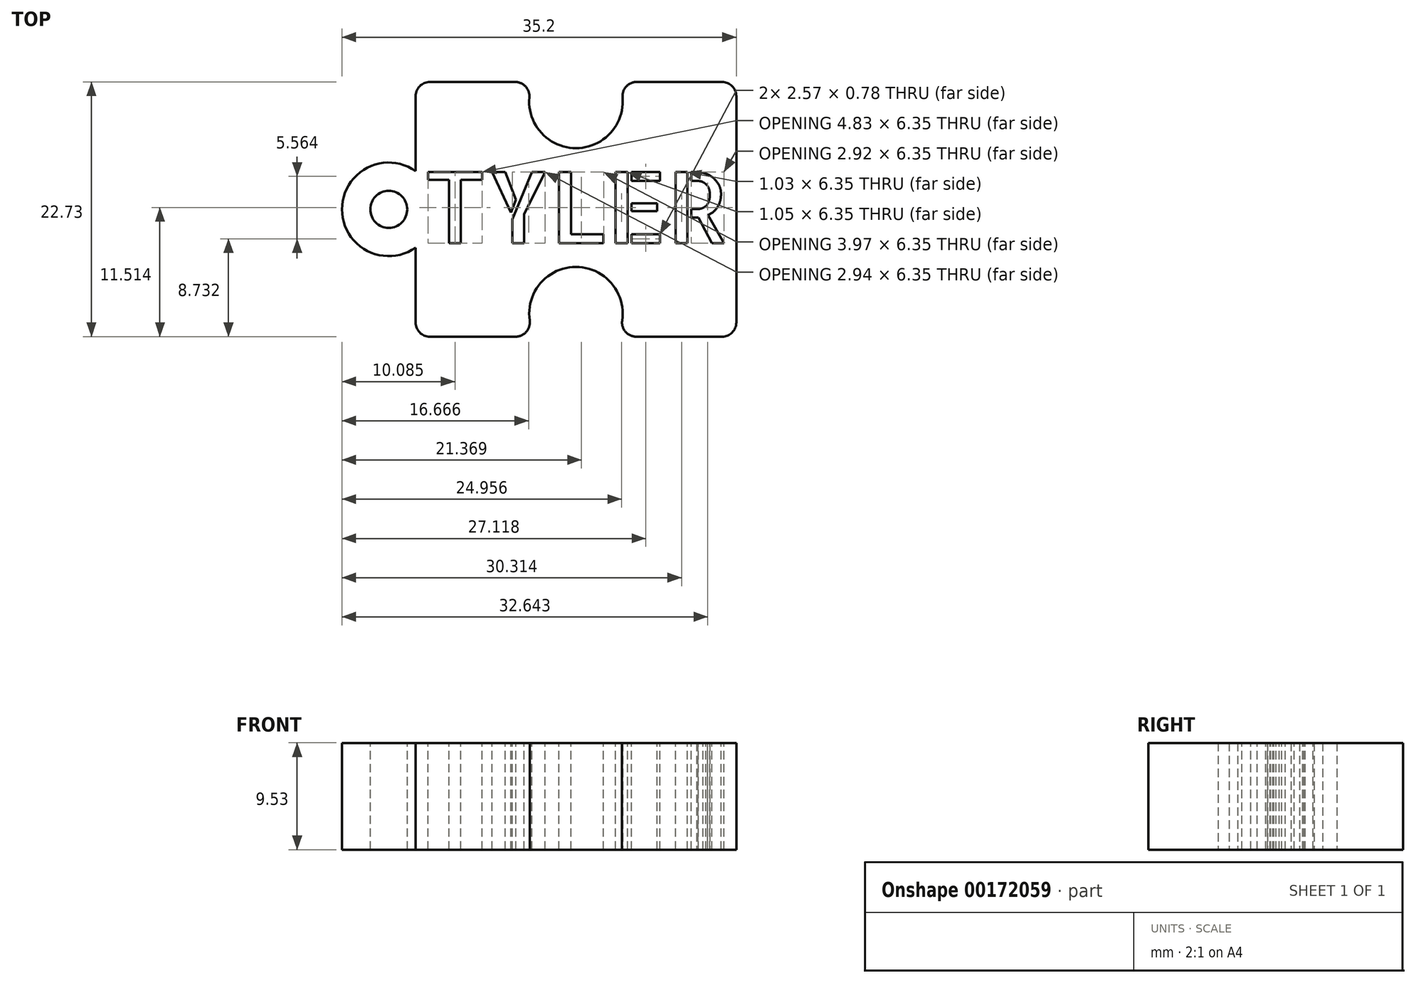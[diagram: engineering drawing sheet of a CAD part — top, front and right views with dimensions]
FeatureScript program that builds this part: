
annotation { "Feature Type Name" : "Feature", "Feature Type Description" : "" }
export const myFeature = defineFeature(function(context is Context, id is Id, definition is map)
    precondition{}
    {
        {
            var Q0;
            Q0=qCreatedBy(makeId("Top.planeOp"),FACE);
            var sketch = newSketch(context, id + "F0", { "sketchPlane" : qUnion([Q0])});
            skLineSegment(sketch, "E0.bottom", {"start": v(-24.82, 39.35) * mm, "end": v(-17.2, 39.35) * mm});
            skLineSegment(sketch, "E0.top", {"start": v(-24.82, 16.62) * mm, "end": v(-17.16, 16.62) * mm});
            skLineSegment(sketch, "E0.left", {"start": v(-26.09, 38.08) * mm, "end": v(-26.09, 31.4) * mm});
            skLineSegment(sketch, "E0.right", {"start": v(2.54, 38.08) * mm, "end": v(2.54, 17.89) * mm});
            skArc(sketch, "E1", {"start": v(-26.09, 31.4) * mm, "mid": v(-32.66, 27.98) * mm, "end": v(-26.09, 24.56) * mm});
            skArc(sketch, "E2", {"start": v(-7.65, 18.07) * mm, "mid": v(-11.78, 22.84) * mm, "end": v(-15.9, 18.07) * mm});
            skArc(sketch, "E3", {"start": v(-15.93, 37.97) * mm, "mid": v(-11.78, 33.44) * mm, "end": v(-7.62, 37.97) * mm});
            skLineSegment(sketch, "E4.trimOffspring", {"start": v(-6.35, 39.35) * mm, "end": v(1.27, 39.35) * mm});
            skLineSegment(sketch, "E5.trimOffspring", {"start": v(-6.39, 16.62) * mm, "end": v(1.27, 16.62) * mm});
            skLineSegment(sketch, "E6.trimOffspring", {"start": v(-26.09, 24.56) * mm, "end": v(-26.09, 17.89) * mm});
            skPoint(sketch, "E7", {"position": v(-11.78, 39.35) * mm});
            skPoint(sketch, "E8", {"position": v(-11.78, 16.62) * mm});
            skLineSegment(sketch, "E9", {"start": v(-11.78, 39.35) * mm, "end": v(-11.78, 16.62) * mm, "construction": true});
            skPoint(sketch, "E10.visualSharp", {"position": v(-26.09, 16.62) * mm});
            skArc(sketch, "E10.filletArc", {"start": v(-26.09, 17.89) * mm, "mid": v(-25.72, 16.99) * mm, "end": v(-24.82, 16.62) * mm});
            skPoint(sketch, "E11.visualSharp", {"position": v(-26.09, 39.35) * mm});
            skArc(sketch, "E11.filletArc", {"start": v(-24.82, 39.35) * mm, "mid": v(-25.72, 38.97) * mm, "end": v(-26.09, 38.08) * mm});
            skPoint(sketch, "E12.visualSharp", {"position": v(2.54, 39.35) * mm});
            skArc(sketch, "E12.filletArc", {"start": v(2.54, 38.08) * mm, "mid": v(2.16, 38.97) * mm, "end": v(1.27, 39.35) * mm});
            skPoint(sketch, "E13.visualSharp", {"position": v(2.54, 16.62) * mm});
            skArc(sketch, "E13.filletArc", {"start": v(1.27, 16.62) * mm, "mid": v(2.16, 16.99) * mm, "end": v(2.54, 17.89) * mm});
            skPoint(sketch, "E14.visualSharp", {"position": v(-8.14, 16.62) * mm});
            skArc(sketch, "E14.filletArc", {"start": v(-7.65, 18.07) * mm, "mid": v(-7.35, 17.05) * mm, "end": v(-6.39, 16.62) * mm});
            skPoint(sketch, "E15.visualSharp", {"position": v(-15.4, 16.62) * mm});
            skArc(sketch, "E15.filletArc", {"start": v(-17.16, 16.62) * mm, "mid": v(-16.2, 17.05) * mm, "end": v(-15.9, 18.07) * mm});
            skPoint(sketch, "E16.visualSharp", {"position": v(-7.98, 39.35) * mm});
            skArc(sketch, "E16.filletArc", {"start": v(-6.35, 39.35) * mm, "mid": v(-7.29, 38.93) * mm, "end": v(-7.62, 37.97) * mm});
            skPoint(sketch, "E17.visualSharp", {"position": v(-15.57, 39.35) * mm});
            skArc(sketch, "E17.filletArc", {"start": v(-15.93, 37.97) * mm, "mid": v(-16.26, 38.93) * mm, "end": v(-17.2, 39.35) * mm});
            skSolve(sketch);
        }
        {
            var Q0;
            Q0 = qSketchRegion(id + "F0", true);
            extrude(context, id + "F1", {"entities" : qUnion([Q0]), "depth" : 9.52 * mm});
        }
        {
            var Q0;
            Q0=makeQuery(id+"F1.opExtrude","CAP_FACE",FACE,{"disambiguationData":[OSD([sQuery(id+"F0.wireOp",EDGE,"E0.bottom"),sQuery(id+"F0.wireOp",EDGE,"E0.top"),sQuery(id+"F0.wireOp",EDGE,"E0.left"),sQuery(id+"F0.wireOp",EDGE,"E0.right"),sQuery(id+"F0.wireOp",EDGE,"E1"),sQuery(id+"F0.wireOp",EDGE,"E2"),sQuery(id+"F0.wireOp",EDGE,"E3"),sQuery(id+"F0.wireOp",EDGE,"E4.trimOffspring"),sQuery(id+"F0.wireOp",EDGE,"E5.trimOffspring"),sQuery(id+"F0.wireOp",EDGE,"E6.trimOffspring"),sQuery(id+"F0.wireOp",EDGE,"E10.filletArc"),sQuery(id+"F0.wireOp",EDGE,"E11.filletArc"),sQuery(id+"F0.wireOp",EDGE,"E12.filletArc"),sQuery(id+"F0.wireOp",EDGE,"E13.filletArc"),sQuery(id+"F0.wireOp",EDGE,"E14.filletArc"),sQuery(id+"F0.wireOp",EDGE,"E15.filletArc"),sQuery(id+"F0.wireOp",EDGE,"E16.filletArc"),sQuery(id+"F0.wireOp",EDGE,"E17.filletArc")])],"isStart":false});
            var sketch = newSketch(context, id + "F2", { "sketchPlane" : qUnion([Q0])});
            skText(sketch, "E18", { "text": "TYLER", "fontName": "AllertaStencil-Regular.ttf"});
            skCircle(sketch, "E19", {"center": v(-28.48, 27.98) * mm, "radius": 1.65 * mm});
            const initialGuessF2  = {"E18": [-0.02543, 0.02496, 1, 0, 0.00635]};
            skSetInitialGuess(sketch, initialGuessF2);
            skSolve(sketch);
        }
        {
            var Q0;
            Q0 = qSketchRegion(id + "F2", true);
            extrude(context, id + "F3", {"entities" : qUnion([Q0]), "operationType" : NewBodyOperationType.REMOVE, "oppositeDirection" : true, "depth" : 25.4 * mm});
        }
    });
